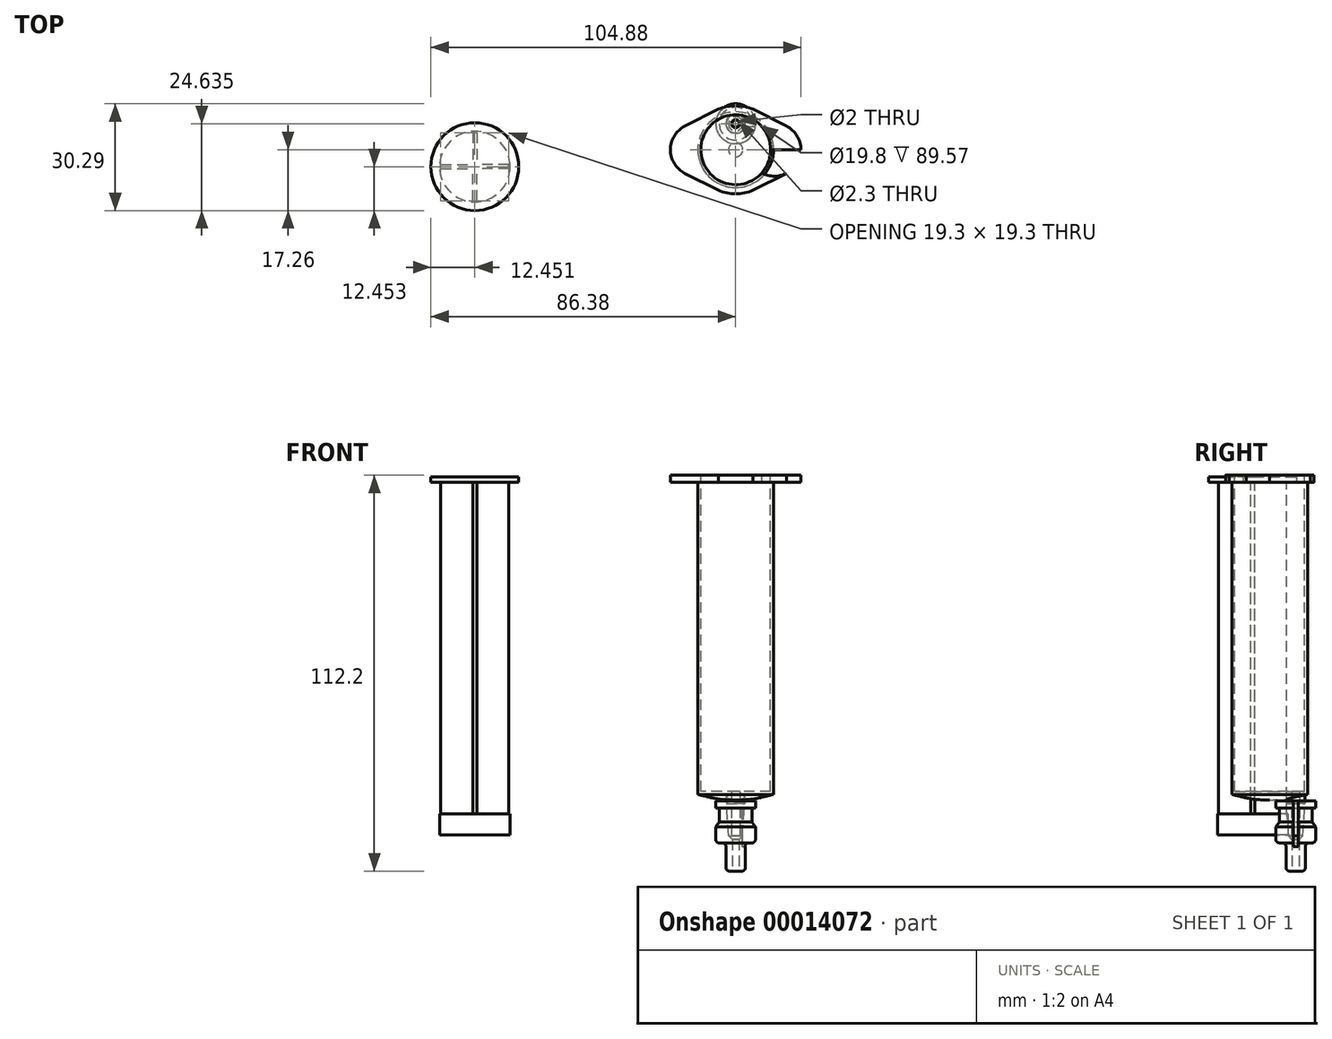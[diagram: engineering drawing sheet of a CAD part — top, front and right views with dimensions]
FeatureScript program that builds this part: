
annotation { "Feature Type Name" : "Feature", "Feature Type Description" : "" }
export const myFeature = defineFeature(function(context is Context, id is Id, definition is map)
    precondition{}
    {
        {
            var Q0;
            Q0=qCreatedBy(makeId("Top.planeOp"),FACE);
            var sketch = newSketch(context, id + "F0", { "sketchPlane" : qUnion([Q0])});
            skCircle(sketch, "E0", {"center": v(0, 0) * mm, "radius": 12.5 * mm});
            skLineSegment(sketch, "E1", {"start": v(0, 0) * mm, "end": v(18.5, 0) * mm});
            skLineSegment(sketch, "E2", {"start": v(0, 0) * mm, "end": v(0, -12.5) * mm});
            skCircle(sketch, "E3", {"center": v(11, 0) * mm, "radius": 7.5 * mm});
            skLineSegment(sketch, "E4", {"start": v(11, 0) * mm, "end": v(18.5, 0) * mm});
            skLineSegment(sketch, "E5", {"start": v(4.94, 11.48) * mm, "end": v(6.35, 10.77) * mm});
            skLineSegment(sketch, "E6.0.MirrorCS", {"start": v(4.94, -11.48) * mm, "end": v(6.35, -10.77) * mm});
            skPoint(sketch, "E7.orphan", {"position": v(12.64, 7.58) * mm});
            skPoint(sketch, "E8.orphan", {"position": v(12.64, -7.58) * mm});
            skLineSegment(sketch, "E9", {"start": v(4.94, 11.48) * mm, "end": v(14.4, 6.69) * mm});
            skLineSegment(sketch, "E10.0.MirrorCS", {"start": v(4.94, -11.48) * mm, "end": v(14.4, -6.69) * mm});
            skLineSegment(sketch, "E11.0.MirrorCS", {"start": v(-4.94, 11.48) * mm, "end": v(-14.4, 6.69) * mm});
            skCircle(sketch, "E12.0.MirrorC", {"center": v(-11, 0) * mm, "radius": 7.5 * mm});
            skLineSegment(sketch, "E13.0.MirrorCS", {"start": v(-4.94, -11.48) * mm, "end": v(-14.4, -6.69) * mm});
            skSolve(sketch);
        }
        {
            var Q0;
            {var subQ0=sQuery(id+"F0.wireOp",EDGE,"E12.0.MirrorC");var subQ3=sQuery(id+"F0.wireOp",EDGE,"E0");var subQ5=makeQuery(id+"F0.imprint","INTERSECT",VERTEX,{"disambiguationData":[OD(0.0)],"derivedFrom":[subQ3,subQ0]});Q0=makeQuery(id+"F0.imprint","IMPRINT",FACE,{"disambiguationData":[TD([[makeQuery(id+"F0.imprint","IMPRINT",EDGE,{"disambiguationData":[TD([[subQ5,-1.0]])],"derivedFrom":subQ3}),-1.0]])]});}
            var Q1;
            {var subQ1=sQuery(id+"F0.wireOp",EDGE,"E0");var subQ3=sQuery(id+"F0.wireOp",EDGE,"E11.0.MirrorCS");var subQ5=makeQuery(id+"F0.imprint","INTERSECT",VERTEX,{"disambiguationData":[OD(1.0)],"derivedFrom":[subQ1,subQ3]});Q1=makeQuery(id+"F0.imprint","IMPRINT",FACE,{"disambiguationData":[TD([[makeQuery(id+"F0.imprint","IMPRINT",EDGE,{"disambiguationData":[TD([[subQ5,-1.0]])],"derivedFrom":subQ1}),-1.0]])]});}
            var Q2;
            {var subQ0=sQuery(id+"F0.wireOp",EDGE,"E12.0.MirrorC");var subQ1=sQuery(id+"F0.wireOp",EDGE,"E0");var subQ3=makeQuery(id+"F0.imprint","INTERSECT",VERTEX,{"disambiguationData":[OD(0.0)],"derivedFrom":[subQ1,subQ0]});Q2=makeQuery(id+"F0.imprint","IMPRINT",FACE,{"disambiguationData":[TD([[makeQuery(id+"F0.imprint","IMPRINT",EDGE,{"disambiguationData":[TD([[subQ3,-1.0]])],"derivedFrom":subQ1}),1.0]])]});}
            var Q3;
            {var subQ0=sQuery(id+"F0.wireOp",EDGE,"E13.0.MirrorCS");var subQ1=sQuery(id+"F0.wireOp",EDGE,"E0");var subQ2=makeQuery(id+"F0.imprint","INTERSECT",VERTEX,{"disambiguationData":[OD(1.0)],"derivedFrom":[subQ1,subQ0]});Q3=makeQuery(id+"F0.imprint","IMPRINT",FACE,{"disambiguationData":[TD([[makeQuery(id+"F0.imprint","IMPRINT",EDGE,{"disambiguationData":[TD([[subQ2,1.0]])],"derivedFrom":subQ1}),-1.0]])]});}
            var Q4;
            {var subQ16=sQuery(id+"F0.wireOp",EDGE,"E2");Q4=makeQuery(id+"F0.imprint","IMPRINT",FACE,{"disambiguationData":[TD([[makeQuery(id+"F0.imprint","IMPRINT",EDGE,{"derivedFrom":subQ16}),-1.0]])]});}
            var Q5;
            {var subQ8=sQuery(id+"F0.wireOp",EDGE,"E2");Q5=makeQuery(id+"F0.imprint","IMPRINT",FACE,{"disambiguationData":[TD([[makeQuery(id+"F0.imprint","IMPRINT",EDGE,{"derivedFrom":subQ8}),1.0]])]});}
            var Q6;
            {var subQ0=sQuery(id+"F0.wireOp",EDGE,"E4");var subQ1=sQuery(id+"F0.wireOp",EDGE,"E0");var subQ2=makeQuery(id+"F0.imprint","INTERSECT",VERTEX,{"derivedFrom":[subQ1,subQ0]});Q6=makeQuery(id+"F0.imprint","IMPRINT",FACE,{"disambiguationData":[TD([[makeQuery(id+"F0.imprint","IMPRINT",EDGE,{"disambiguationData":[TD([[subQ2,1.0]])],"derivedFrom":subQ1}),1.0]])]});}
            var Q7;
            {var subQ0=sQuery(id+"F0.wireOp",EDGE,"E9");var subQ1=sQuery(id+"F0.wireOp",EDGE,"E0");var subQ2=makeQuery(id+"F0.imprint","INTERSECT",VERTEX,{"disambiguationData":[OD(1.0)],"derivedFrom":[subQ1,subQ0]});Q7=makeQuery(id+"F0.imprint","IMPRINT",FACE,{"disambiguationData":[TD([[makeQuery(id+"F0.imprint","IMPRINT",EDGE,{"disambiguationData":[TD([[subQ2,1.0]])],"derivedFrom":subQ1}),-1.0]])]});}
            var Q8;
            {var subQ1=sQuery(id+"F0.wireOp",EDGE,"E0");var subQ3=sQuery(id+"F0.wireOp",EDGE,"E3");var subQ5=makeQuery(id+"F0.imprint","INTERSECT",VERTEX,{"disambiguationData":[OD(0.0)],"derivedFrom":[subQ1,subQ3]});Q8=makeQuery(id+"F0.imprint","IMPRINT",FACE,{"disambiguationData":[TD([[makeQuery(id+"F0.imprint","IMPRINT",EDGE,{"disambiguationData":[TD([[subQ5,1.0]])],"derivedFrom":subQ1}),-1.0]])]});}
            var Q9;
            {var subQ0=sQuery(id+"F0.wireOp",EDGE,"E4");var subQ1=sQuery(id+"F0.wireOp",EDGE,"E0");var subQ2=makeQuery(id+"F0.imprint","INTERSECT",VERTEX,{"derivedFrom":[subQ1,subQ0]});Q9=makeQuery(id+"F0.imprint","IMPRINT",FACE,{"disambiguationData":[TD([[makeQuery(id+"F0.imprint","IMPRINT",EDGE,{"disambiguationData":[TD([[subQ2,1.0]])],"derivedFrom":subQ1}),-1.0]])]});}
            var Q10;
            {var subQ0=sQuery(id+"F0.wireOp",EDGE,"E10.0.MirrorCS");var subQ1=sQuery(id+"F0.wireOp",EDGE,"E0");var subQ2=makeQuery(id+"F0.imprint","INTERSECT",VERTEX,{"disambiguationData":[OD(1.0)],"derivedFrom":[subQ1,subQ0]});Q10=makeQuery(id+"F0.imprint","IMPRINT",FACE,{"disambiguationData":[TD([[makeQuery(id+"F0.imprint","IMPRINT",EDGE,{"disambiguationData":[TD([[subQ2,-1.0]])],"derivedFrom":subQ1}),-1.0]])]});}
            var Q11;
            {var subQ1=sQuery(id+"F0.wireOp",EDGE,"E0");var subQ5=sQuery(id+"F0.wireOp",EDGE,"E3");var subQ7=makeQuery(id+"F0.imprint","INTERSECT",VERTEX,{"disambiguationData":[OD(0.0)],"derivedFrom":[subQ1,subQ5]});Q11=makeQuery(id+"F0.imprint","IMPRINT",FACE,{"disambiguationData":[TD([[makeQuery(id+"F0.imprint","IMPRINT",EDGE,{"disambiguationData":[TD([[subQ7,1.0]])],"derivedFrom":subQ1}),1.0]])]});}
            extrude(context, id + "F1", {"entities" : qUnion([Q0, Q1, Q2, Q3, Q4, Q5, Q6, Q7, Q8, Q9, Q10, Q11]), "depth" : 2 * mm});
        }
        {
            var Q0;
            Q0=makeQuery(id+"F1.opExtrude","CAP_FACE",FACE,{"disambiguationData":[OSD([sQuery(id+"F0.wireOp",EDGE,"E0"),sQuery(id+"F0.wireOp",EDGE,"E3"),sQuery(id+"F0.wireOp",EDGE,"E9"),sQuery(id+"F0.wireOp",EDGE,"E10.0.MirrorCS"),sQuery(id+"F0.wireOp",EDGE,"E11.0.MirrorCS"),sQuery(id+"F0.wireOp",EDGE,"E12.0.MirrorC"),sQuery(id+"F0.wireOp",EDGE,"E13.0.MirrorCS")])],"isStart":true});
            var sketch = newSketch(context, id + "F2", { "sketchPlane" : qUnion([Q0])});
            skCircle(sketch, "E14", {"center": v(0, 0) * mm, "radius": 10.72 * mm});
            skSolve(sketch);
        }
        {
            var Q0;
            Q0 = qSketchRegion(id + "F2", true);
            extrude(context, id + "F3", {"entities" : qUnion([Q0]), "operationType" : NewBodyOperationType.ADD, "depth" : 88.5 * mm});
        }
        {
            var Q0;
            Q0=qCreatedBy(makeId("Front.planeOp"),FACE);
            var sketch = newSketch(context, id + "F4", { "sketchPlane" : qUnion([Q0])});
            skLineSegment(sketch, "E15.0", {"start": v(10.72, -88.5) * mm, "end": v(-10.72, -88.5) * mm});
            skPoint(sketch, "E16", {"position": v(0, -88.5) * mm});
            skLineSegment(sketch, "E17", {"start": v(0, -88.5) * mm, "end": v(0, -90) * mm});
            skLineSegment(sketch, "E18", {"start": v(0, -90) * mm, "end": v(2, -90) * mm});
            skFitSpline(sketch, "E19", {"points": [v(2, -90) * mm, v(10.72, -88.5) * mm], "startDerivative": vector(12.47, 0.23) * mm, "endDerivative": vector(8.73, 1.5) * mm});
            skSolve(sketch);
        }
        {
            var Q0;
            Q0 = qSketchRegion(id + "F4", true);
            var Q1;
            Q1=sQuery(id+"F4.wireOp",EDGE,"E17");
            revolve(context, id + "F5", {"operationType" : NewBodyOperationType.ADD, "entities" : qUnion([Q0]), "axis" : qUnion([Q1]), "revolveType" : RevolveType.FULL});
        }
        {
            var Q0;
            Q0=makeQuery(id+"F1.opExtrude","CAP_FACE",FACE,{"disambiguationData":[OSD([sQuery(id+"F0.wireOp",EDGE,"E0"),sQuery(id+"F0.wireOp",EDGE,"E3"),sQuery(id+"F0.wireOp",EDGE,"E9"),sQuery(id+"F0.wireOp",EDGE,"E10.0.MirrorCS"),sQuery(id+"F0.wireOp",EDGE,"E11.0.MirrorCS"),sQuery(id+"F0.wireOp",EDGE,"E12.0.MirrorC"),sQuery(id+"F0.wireOp",EDGE,"E13.0.MirrorCS")])],"isStart":false});
            var sketch = newSketch(context, id + "F6", { "sketchPlane" : qUnion([Q0])});
            skCircle(sketch, "E20", {"center": v(0, 0) * mm, "radius": 9.9 * mm});
            skSolve(sketch);
        }
        {
            var Q0;
            Q0=makeQuery(id+"F6.imprint","IMPRINT",FACE,{"disambiguationData":[TD([[makeQuery(id+"F6.imprint","IMPRINT",EDGE,{"derivedFrom":sQuery(id+"F6.wireOp",EDGE,"E20")}),1.0]])]});
            extrude(context, id + "F7", {"entities" : qUnion([Q0]), "operationType" : NewBodyOperationType.REMOVE, "oppositeDirection" : true, "depth" : 89.57 * mm});
        }
        {
            var Q0;
            Q0=qCreatedBy(makeId("Top.planeOp"),FACE);
            var sketch = newSketch(context, id + "F8", { "sketchPlane" : qUnion([Q0])});
            skCircle(sketch, "E21", {"center": v(-73.93, -4.8) * mm, "radius": 12.45 * mm});
            skSolve(sketch);
        }
        {
            var Q0;
            Q0 = qSketchRegion(id + "F8", true);
            extrude(context, id + "F9", {"entities" : qUnion([Q0]), "depth" : 1.5 * mm});
        }
        {
            var Q0;
            Q0=makeQuery(id+"F9.opExtrude","CAP_FACE",FACE,{"disambiguationData":[OSD([sQuery(id+"F8.wireOp",EDGE,"E21")])],"isStart":true});
            var sketch = newSketch(context, id + "F10", { "sketchPlane" : qUnion([Q0])});
            skLineSegment(sketch, "E22", {"start": v(-73.93, 4.8) * mm, "end": v(-64.28, 4.8) * mm});
            skLineSegment(sketch, "E23", {"start": v(-73.93, 4.8) * mm, "end": v(-73.93, 10.47) * mm, "construction": true});
            skLineSegment(sketch, "E24", {"start": v(-64.28, 4.8) * mm, "end": v(-64.28, 5.4) * mm});
            skLineSegment(sketch, "E25", {"start": v(-64.28, 5.4) * mm, "end": v(-73.93, 5.4) * mm});
            skLineSegment(sketch, "E26.0.MirrorCS", {"start": v(-64.28, 4.2) * mm, "end": v(-73.93, 4.2) * mm});
            skLineSegment(sketch, "E27.0.MirrorCS", {"start": v(-64.28, 4.8) * mm, "end": v(-64.28, 4.2) * mm});
            skLineSegment(sketch, "E28.0.MirrorCS", {"start": v(-83.58, 5.4) * mm, "end": v(-73.93, 5.4) * mm});
            skLineSegment(sketch, "E29.0.MirrorCS", {"start": v(-83.58, 4.2) * mm, "end": v(-73.93, 4.2) * mm});
            skLineSegment(sketch, "E30.0.MirrorCS", {"start": v(-73.93, 4.8) * mm, "end": v(-83.58, 4.8) * mm});
            skLineSegment(sketch, "E31.0.MirrorCS", {"start": v(-83.58, 4.8) * mm, "end": v(-83.58, 5.4) * mm});
            skLineSegment(sketch, "E32.0.MirrorCS", {"start": v(-83.58, 4.8) * mm, "end": v(-83.58, 4.2) * mm});
            skLineSegment(sketch, "E33", {"start": v(-73.93, 4.8) * mm, "end": v(-69.39, 9.35) * mm, "construction": true});
            skLineSegment(sketch, "E34.0.MirrorCS", {"start": v(-73.93, -4.84) * mm, "end": v(-73.33, -4.84) * mm});
            skLineSegment(sketch, "E35.0.MirrorCS", {"start": v(-73.93, -4.84) * mm, "end": v(-74.53, -4.84) * mm});
            skLineSegment(sketch, "E36.0.MirrorCS", {"start": v(-74.53, -4.84) * mm, "end": v(-74.53, 4.8) * mm});
            skLineSegment(sketch, "E37.0.MirrorCS", {"start": v(-73.33, -4.84) * mm, "end": v(-73.33, 4.8) * mm});
            skLineSegment(sketch, "E38.0.MirrorCS", {"start": v(-73.33, 14.46) * mm, "end": v(-73.33, 4.8) * mm});
            skLineSegment(sketch, "E39.0.MirrorCS", {"start": v(-74.53, 14.46) * mm, "end": v(-74.53, 4.8) * mm});
            skLineSegment(sketch, "E40.0.MirrorCS", {"start": v(-73.93, 14.46) * mm, "end": v(-73.33, 14.46) * mm});
            skLineSegment(sketch, "E41.0.MirrorCS", {"start": v(-73.93, 14.46) * mm, "end": v(-74.53, 14.46) * mm});
            skSolve(sketch);
        }
        {
            var Q0;
            {var subQ7=sQuery(id+"F10.wireOp",EDGE,"E40.0.MirrorCS");Q0=makeQuery(id+"F10.imprint","IMPRINT",FACE,{"disambiguationData":[TD([[makeQuery(id+"F10.imprint","IMPRINT",EDGE,{"derivedFrom":subQ7}),-1.0]])]});}
            var Q1;
            {var subQ5=sQuery(id+"F10.wireOp",EDGE,"E32.0.MirrorCS");Q1=makeQuery(id+"F10.imprint","IMPRINT",FACE,{"disambiguationData":[TD([[makeQuery(id+"F10.imprint","IMPRINT",EDGE,{"derivedFrom":subQ5}),1.0]])]});}
            var Q2;
            {var subQ5=sQuery(id+"F10.wireOp",EDGE,"E31.0.MirrorCS");Q2=makeQuery(id+"F10.imprint","IMPRINT",FACE,{"disambiguationData":[TD([[makeQuery(id+"F10.imprint","IMPRINT",EDGE,{"derivedFrom":subQ5}),-1.0]])]});}
            var Q3;
            {var subQ1=sQuery(id+"F10.wireOp",EDGE,"E28.0.MirrorCS");var subQ6=sQuery(id+"F10.wireOp",EDGE,"E25");var subQ11=makeQuery(id+"F10.imprint","INTERSECT",VERTEX,{"derivedFrom":[subQ6,subQ1]});Q3=makeQuery(id+"F10.imprint","IMPRINT",FACE,{"disambiguationData":[TD([[makeQuery(id+"F10.imprint","IMPRINT",EDGE,{"disambiguationData":[TD([[subQ11,1.0]])],"derivedFrom":subQ6}),1.0]])]});}
            var Q4;
            {var subQ1=sQuery(id+"F10.wireOp",EDGE,"E29.0.MirrorCS");var subQ7=sQuery(id+"F10.wireOp",EDGE,"E26.0.MirrorCS");var subQ8=makeQuery(id+"F10.imprint","INTERSECT",VERTEX,{"derivedFrom":[subQ7,subQ1]});Q4=makeQuery(id+"F10.imprint","IMPRINT",FACE,{"disambiguationData":[TD([[makeQuery(id+"F10.imprint","IMPRINT",EDGE,{"disambiguationData":[TD([[subQ8,1.0]])],"derivedFrom":subQ7}),-1.0]])]});}
            var Q5;
            {var subQ4=sQuery(id+"F10.wireOp",EDGE,"E34.0.MirrorCS");Q5=makeQuery(id+"F10.imprint","IMPRINT",FACE,{"disambiguationData":[TD([[makeQuery(id+"F10.imprint","IMPRINT",EDGE,{"derivedFrom":subQ4}),1.0]])]});}
            var Q6;
            {var subQ5=sQuery(id+"F10.wireOp",EDGE,"E27.0.MirrorCS");Q6=makeQuery(id+"F10.imprint","IMPRINT",FACE,{"disambiguationData":[TD([[makeQuery(id+"F10.imprint","IMPRINT",EDGE,{"derivedFrom":subQ5}),-1.0]])]});}
            var Q7;
            {var subQ5=sQuery(id+"F10.wireOp",EDGE,"E24");Q7=makeQuery(id+"F10.imprint","IMPRINT",FACE,{"disambiguationData":[TD([[makeQuery(id+"F10.imprint","IMPRINT",EDGE,{"derivedFrom":subQ5}),1.0]])]});}
            extrude(context, id + "F11", {"entities" : qUnion([Q0, Q1, Q2, Q3, Q4, Q5, Q6, Q7]), "operationType" : NewBodyOperationType.ADD, "depth" : 95 * mm});
        }
        {
            var Q0;
            Q0=makeQuery(id+"F11.opExtrude","CAP_FACE",FACE,{"disambiguationData":[OSD([sQuery(id+"F10.wireOp",EDGE,"E24"),sQuery(id+"F10.wireOp",EDGE,"E25"),sQuery(id+"F10.wireOp",EDGE,"E26.0.MirrorCS"),sQuery(id+"F10.wireOp",EDGE,"E27.0.MirrorCS"),sQuery(id+"F10.wireOp",EDGE,"E28.0.MirrorCS"),sQuery(id+"F10.wireOp",EDGE,"E29.0.MirrorCS"),sQuery(id+"F10.wireOp",EDGE,"E31.0.MirrorCS"),sQuery(id+"F10.wireOp",EDGE,"E32.0.MirrorCS"),sQuery(id+"F10.wireOp",EDGE,"E34.0.MirrorCS"),sQuery(id+"F10.wireOp",EDGE,"E35.0.MirrorCS"),sQuery(id+"F10.wireOp",EDGE,"E36.0.MirrorCS"),sQuery(id+"F10.wireOp",EDGE,"E37.0.MirrorCS"),sQuery(id+"F10.wireOp",EDGE,"E38.0.MirrorCS"),sQuery(id+"F10.wireOp",EDGE,"E39.0.MirrorCS"),sQuery(id+"F10.wireOp",EDGE,"E40.0.MirrorCS"),sQuery(id+"F10.wireOp",EDGE,"E41.0.MirrorCS")])],"isStart":false});
            var sketch = newSketch(context, id + "F12", { "sketchPlane" : qUnion([Q0])});
            skLineSegment(sketch, "E42", {"start": v(-74.53, 4.2) * mm, "end": v(-73.33, 4.2) * mm});
            skLineSegment(sketch, "E43", {"start": v(-73.33, 4.2) * mm, "end": v(-74.53, 5.4) * mm});
            skCircle(sketch, "E44", {"center": v(-73.93, 4.8) * mm, "radius": 10 * mm});
            skSolve(sketch);
        }
        {
            var Q0;
            Q0 = qSketchRegion(id + "F12", true);
            extrude(context, id + "F13", {"entities" : qUnion([Q0]), "operationType" : NewBodyOperationType.ADD, "oppositeDirection" : true, "depth" : 1 * mm, "hasSecondDirection" : true, "secondDirectionOppositeDirection" : false, "secondDirectionDepth" : 5 * mm});
        }
        {
            var Q0;
            Q0=qCreatedBy(makeId("Top.planeOp"),FACE);
            cPlane(context, id + "F14", {"entities" : qUnion([Q0]), "cplaneType" : CPlaneType.OFFSET, "offset" : 88 * mm, "oppositeDirection" : true, "width" : 150 * mm, "height" : 150 * mm});
        }
        {
            var Q0;
            Q0=qCreatedBy(id+"F14.planeOp",FACE);
            var sketch = newSketch(context, id + "F15", { "sketchPlane" : qUnion([Q0])});
            skCircle(sketch, "E45.0", {"center": v(0, 0) * mm, "radius": 10.72 * mm, "construction": true});
            skLineSegment(sketch, "E46", {"start": v(0, 10.72) * mm, "end": v(0, 10.03) * mm});
            skCircle(sketch, "E47", {"center": v(0, 7.38) * mm, "radius": 2.65 * mm});
            skLineSegment(sketch, "E48", {"start": v(0, 7.38) * mm, "end": v(0, 10.02) * mm});
            skSolve(sketch);
        }
        {
            var Q0;
            Q0 = qSketchRegion(id + "F15", true);
            extrude(context, id + "F16", {"entities" : qUnion([Q0]), "operationType" : NewBodyOperationType.ADD, "oppositeDirection" : true, "depth" : 3 * mm});
        }
        {
            var Q0;
            Q0=makeQuery(id+"F16.opExtrude","CAP_FACE",FACE,{"disambiguationData":[OSD([sQuery(id+"F15.wireOp",EDGE,"E47")])],"isStart":false});
            cPlane(context, id + "F17", {"entities" : qUnion([Q0]), "cplaneType" : CPlaneType.OFFSET, "offset" : 9.2 * mm, "width" : 150 * mm, "height" : 150 * mm});
        }
        {
            var Q0;
            Q0=qCreatedBy(id+"F17.planeOp",FACE);
            var sketch = newSketch(context, id + "F18", { "sketchPlane" : qUnion([Q0])});
            skCircle(sketch, "E49.0", {"center": v(0, -7.38) * mm, "radius": 2.65 * mm, "construction": true});
            skCircle(sketch, "E50", {"center": v(0, -7.38) * mm, "radius": 2 * mm});
            skSolve(sketch);
        }
        {
            var Q1;
            Q1=makeQuery(id+"F16.opExtrude","CAP_FACE",FACE,{"disambiguationData":[OSD([sQuery(id+"F15.wireOp",EDGE,"E47")])],"isStart":false});
            var Q2;
            Q2=makeQuery(id+"F18.imprint","IMPRINT",FACE,{"disambiguationData":[TD([[makeQuery(id+"F18.imprint","IMPRINT",EDGE,{"derivedFrom":sQuery(id+"F18.wireOp",EDGE,"E50")}),1.0]])]});
            loft(context, id + "F19", {"operationType" : NewBodyOperationType.ADD, "sheetProfilesArray" : [{ "sheetProfileEntities" : qUnion([Q1]) }, { "sheetProfileEntities" : qUnion([Q2]) }]});
        }
        {
            var Q0;
            Q0=makeQuery(id+"F19.opLoft","CAP_FACE",FACE,{"disambiguationData":[OSD([makeQuery(id+"F18.imprint","IMPRINT",FACE,{"disambiguationData":[TD([[makeQuery(id+"F18.imprint","IMPRINT",EDGE,{"derivedFrom":sQuery(id+"F18.wireOp",EDGE,"E50")}),1.0]])]})])],"isStart":true});
            var sketch = newSketch(context, id + "F20", { "sketchPlane" : qUnion([Q0])});
            skCircle(sketch, "E51", {"center": v(0, -7.38) * mm, "radius": 1.15 * mm});
            skSolve(sketch);
        }
        {
            var Q0;
            Q0 = qSketchRegion(id + "F20", true);
            extrude(context, id + "F21", {"entities" : qUnion([Q0]), "operationType" : NewBodyOperationType.REMOVE, "endBound" : BoundingType.THROUGH_ALL, "oppositeDirection" : true, "depth" : 25 * mm});
        }
        {
            var Q0;
            Q0=qCreatedBy(makeId("Right.planeOp"),FACE);
            var sketch = newSketch(context, id + "F22", { "sketchPlane" : qUnion([Q0])});
            skLineSegment(sketch, "E52.0", {"start": v(9.38, -100.2) * mm, "end": v(5.38, -100.2) * mm});
            skLineSegment(sketch, "E52.1", {"start": v(10.02, -91) * mm, "end": v(4.72, -91) * mm});
            skLineSegment(sketch, "E53", {"start": v(7.38, -100.2) * mm, "end": v(7.38, -91) * mm, "construction": true});
            skLineSegment(sketch, "E54", {"start": v(4.72, -91) * mm, "end": v(4.72, -90.3) * mm});
            skLineSegment(sketch, "E55", {"start": v(4.72, -90.3) * mm, "end": v(7.38, -90.3) * mm});
            skLineSegment(sketch, "E56", {"start": v(4.72, -90.3) * mm, "end": v(1.72, -90.3) * mm});
            skLineSegment(sketch, "E57", {"start": v(1.72, -90.3) * mm, "end": v(1.72, -100.2) * mm});
            skLineSegment(sketch, "E58", {"start": v(5.38, -102.2) * mm, "end": v(5.38, -100.2) * mm});
            skLineSegment(sketch, "E59", {"start": v(4.73, -91) * mm, "end": v(5.38, -100.2) * mm});
            skLineSegment(sketch, "E60", {"start": v(4.62, -110.2) * mm, "end": v(10.12, -110.2) * mm, "construction": true});
            skLineSegment(sketch, "E61", {"start": v(7.38, -110.2) * mm, "end": v(7.38, -100.2) * mm, "construction": true});
            skLineSegment(sketch, "E62", {"start": v(4.62, -109.2) * mm, "end": v(4.62, -103.2) * mm});
            skPoint(sketch, "E63.visualSharp", {"position": v(3.12, -110.2) * mm});
            skArc(sketch, "E63.filletArc", {"start": v(3.12, -109.7) * mm, "mid": v(3.27, -110.05) * mm, "end": v(3.62, -110.2) * mm});
            skLineSegment(sketch, "E64", {"start": v(4.62, -102.2) * mm, "end": v(7.38, -102.2) * mm, "construction": true});
            skPoint(sketch, "E65.visualSharp", {"position": v(3.12, -102.2) * mm});
            skPoint(sketch, "E66.newPointB", {"position": v(5.38, -102.2) * mm});
            skPoint(sketch, "E67.visualSharp", {"position": v(1.72, -102.2) * mm});
            skLineSegment(sketch, "E68", {"start": v(1.72, -90.3) * mm, "end": v(-1.16, -90.3) * mm});
            skLineSegment(sketch, "E69", {"start": v(-1.16, -90.3) * mm, "end": v(-1.16, -92.3) * mm, "construction": true});
            skLineSegment(sketch, "E70", {"start": v(-1.16, -92.3) * mm, "end": v(1.72, -92.3) * mm});
            skLineSegment(sketch, "E71", {"start": v(1.72, -92.3) * mm, "end": v(2.72, -92.3) * mm});
            skLineSegment(sketch, "E72", {"start": v(2.72, -92.3) * mm, "end": v(2.72, -96.3) * mm});
            skLineSegment(sketch, "E73", {"start": v(2.72, -96.3) * mm, "end": v(1.72, -97.65) * mm});
            skLineSegment(sketch, "E74", {"start": v(5.38, -100.2) * mm, "end": v(6.38, -100.2) * mm});
            skLineSegment(sketch, "E75", {"start": v(6.38, -100.2) * mm, "end": v(6.38, -110.2) * mm});
            skLineSegment(sketch, "E76", {"start": v(6.38, -110.2) * mm, "end": v(5.62, -110.2) * mm});
            skLineSegment(sketch, "E77", {"start": v(3.62, -102.2) * mm, "end": v(2.73, -102.2) * mm});
            skLineSegment(sketch, "E78", {"start": v(1.72, -100.2) * mm, "end": v(1.72, -101.2) * mm});
            skPoint(sketch, "E79.visualSharp", {"position": v(4.62, -110.2) * mm});
            skArc(sketch, "E79.filletArc", {"start": v(4.62, -109.2) * mm, "mid": v(4.92, -109.9) * mm, "end": v(5.62, -110.2) * mm});
            skPoint(sketch, "E80.visualSharp", {"position": v(4.62, -102.2) * mm});
            skArc(sketch, "E80.filletArc", {"start": v(4.62, -103.2) * mm, "mid": v(4.33, -102.5) * mm, "end": v(3.62, -102.2) * mm});
            skArc(sketch, "E81.filletArc", {"start": v(1.72, -101.2) * mm, "mid": v(2.02, -101.9) * mm, "end": v(2.73, -102.2) * mm});
            skLineSegment(sketch, "E82", {"start": v(6.38, -100.2) * mm, "end": v(6.38, -101.2) * mm});
            skLineSegment(sketch, "E83", {"start": v(6.38, -101.2) * mm, "end": v(5.38, -100.2) * mm});
            skSolve(sketch);
        }
        {
            var Q0;
            Q0=makeQuery(id+"F22.imprint","IMPRINT",FACE,{"disambiguationData":[TD([[makeQuery(id+"F22.imprint","IMPRINT",EDGE,{"derivedFrom":sQuery(id+"F22.wireOp",EDGE,"E54")}),1.0]])]});
            var Q1;
            Q1=sQuery(id+"F22.wireOp",EDGE,"E61");
            revolve(context, id + "F23", {"entities" : qUnion([Q0]), "axis" : qUnion([Q1]), "revolveType" : RevolveType.FULL});
        }
        {
            var Q0;
            Q0=makeQuery(id+"F23.opRevolve","SWEPT_FACE",FACE,{"disambiguationData":[OSD([sQuery(id+"F22.wireOp",EDGE,"E56")])]});
            var sketch = newSketch(context, id + "F24", { "sketchPlane" : qUnion([Q0])});
            skLineSegment(sketch, "E84", {"start": v(2.65, 7.4) * mm, "end": v(5.65, 7.4) * mm, "construction": true});
            skLineSegment(sketch, "E85", {"start": v(2.65, 7.4) * mm, "end": v(2.66, 6.65) * mm, "construction": true});
            skCircle(sketch, "E86.0", {"center": v(0, 7.38) * mm, "radius": 2.65 * mm});
            skLineSegment(sketch, "E87", {"start": v(2.66, 6.65) * mm, "end": v(2.55, 6.65) * mm});
            skLineSegment(sketch, "E88", {"start": v(2.55, 6.65) * mm, "end": v(5.6, 6.65) * mm});
            skCircle(sketch, "E89.0", {"center": v(0, 7.38) * mm, "radius": 5.65 * mm});
            skLineSegment(sketch, "E90.0.MirrorCS", {"start": v(2.55, 8.15) * mm, "end": v(5.6, 8.15) * mm});
            skLineSegment(sketch, "E91", {"start": v(5.6, 6.65) * mm, "end": v(6.49, 6.65) * mm});
            skLineSegment(sketch, "E92", {"start": v(6.49, 6.65) * mm, "end": v(6.49, 8.15) * mm});
            skLineSegment(sketch, "E93", {"start": v(6.49, 8.15) * mm, "end": v(5.6, 8.15) * mm});
            skCircle(sketch, "E94.0", {"center": v(0, 7.38) * mm, "radius": 2 * mm});
            skLineSegment(sketch, "E95", {"start": v(2.55, 8.15) * mm, "end": v(1.84, 8.15) * mm});
            skLineSegment(sketch, "E96", {"start": v(2.55, 6.65) * mm, "end": v(1.86, 6.65) * mm});
            skSolve(sketch);
        }
        {
            var Q0;
            {var subQ7=sQuery(id+"F24.wireOp",EDGE,"E88");Q0=makeQuery(id+"F24.imprint","IMPRINT",FACE,{"disambiguationData":[TD([[makeQuery(id+"F24.imprint","IMPRINT",EDGE,{"derivedFrom":subQ7}),1.0]])]});}
            var Q1;
            {var subQ0=sQuery(id+"F24.wireOp",EDGE,"E96");Q1=makeQuery(id+"F24.imprint","IMPRINT",FACE,{"disambiguationData":[TD([[makeQuery(id+"F24.imprint","IMPRINT",EDGE,{"derivedFrom":subQ0}),-1.0]])]});}
            var Q2;
            Q2=makeQuery(id+"F23.opRevolve","SWEPT_FACE",FACE,{"disambiguationData":[OSD([sQuery(id+"F22.wireOp",EDGE,"E77")])]});
            extrude(context, id + "F25", {"entities" : qUnion([Q0, Q1, Q2]), "operationType" : NewBodyOperationType.REMOVE, "oppositeDirection" : true, "depth" : 13 * mm});
        }
    });
